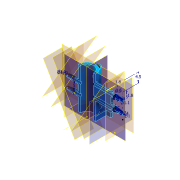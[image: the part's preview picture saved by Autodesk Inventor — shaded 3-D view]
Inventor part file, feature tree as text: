
AUTODESK INVENTOR PART (.ipt)
format: ipt  version: 2021 (Build 250183000, 183)  size: 432,128 bytes
history: native  units: in
note: dims shown in document units (in); Inventor stores cm internally (conversion verified against a paired STEP export)
features: plane x17, sketch x16, extrude x15, projected_geometry x7, mirror x5, revolve x4, split x2, fillet x2, boolean_combine x1
ambient origin geometry x8: Origin, YZ Plane, XZ Plane, XY Plane, X Axis, Y Axis, Z Axis, Center Point
bodies: Solid1 (feature_tree), Solid2 (feature_tree), Solid4 (feature_tree), Solid6 (feature_tree), Solid11 (feature_tree)
feature tree (69):
  extrude  "Extrusion1"  Depth=0.315in
  plane  "Work Plane1"
  sketch  "Sketch2"  dims[d2=0.748in d3=0.0in d4=0.5118in]
  extrude  "Extrusion2"  Depth=0.5118in
  extrude  "Extrusion3"  Depth=0.0709in
  sketch  "Sketch3"  dims[d5=0.0709in d7=0.0709in]
  revolve  "Revolution1"  [1 undecoded]
  revolve  "Revolution3"  [1 undecoded]
  plane  "Work Plane2"
  plane  "Work Plane7"
  extrude  "Extrusion4"  Depth=0.0472in
  extrude  "Extrusion5"  Depth=0.0551in
  sketch  "Sketch6"  dims[d20=0.8268in d21=0.0in d23=0.0472in]
  revolve  "Revolution5"  [1 undecoded]
  plane  "Work Plane8"
  plane  "Work Plane9"
  plane  "Work Plane10"
  plane  "Work Plane14"
  split  "Split7"
  mirror  "Mirror1"
  mirror  "Mirror2"
  revolve  "Revolution9"  Angle=90.0deg
  plane  "Work Plane17"
  extrude  "Extrusion9"  TaperAngle=30.0deg  [1 undecoded]
  plane  "Work Plane18"
  extrude  "Extrusion10"  Depth=0.2756in
  mirror  "Mirror3"
  extrude  "Extrusion16"  Depth=0.0709in
  extrude  "Extrusion17"  Depth=0.0197in
  mirror  "Mirror4"
  mirror  "Mirror5"
  extrude  "Extrusion18"  Depth=0.3937in
  extrude  "Extrusion19"  Depth=0.0551in
  plane  "Work Plane23"
  extrude  "Extrusion20"  Depth=0.0197in
  fillet  "Fillet5"  Radius=0.1969in
  fillet  "Fillet6"  [1 undecoded]
  extrude  "Extrusion21"  Depth=0.3937in
  extrude  "Extrusion22"  TaperAngle=90.0deg  [1 undecoded]
  extrude  "Extrusion23"  [1 undecoded]
  boolean_combine  "Combine1"
  split  "Split10"
  sketch  "Sketch1"  dims[d0=0.2354in d1=0.315in]
  sketch  "Sketch4"  dims[d9=0.1772in d14=0.8268in d15=0.0in]
  sketch  "Sketch5"  dims[d16=0.0197in d18=0.0197in]
  plane  "Work Plane11"
  plane  "Work Plane12"
  plane  "Work Plane13"
  sketch  "Sketch12"  dims[d30=0.0472in d34=0.0551in]
  sketch  "Sketch13"  dims[d35=0.0433in d38=0.0551in]
  plane  "Work Plane19"
  sketch  "Sketch20"  dims[d41=0.0394in d42=90.0deg]
  sketch  "Sketch21"  dims[d44=90.0deg d46=30.0deg]
  plane  "Work Plane20"
  plane  "Work Plane21"
  plane  "Work Plane22"
  sketch  "Sketch22"  dims[d51=-0.2362in d52=0.2756in]
  sketch  "Sketch23"  dims[d53=0.0709in d54=0.0709in]
  sketch  "Sketch24"  dims[d56=0.3937in d57=0.0in d58=0.0197in]
  sketch  "Sketch25"  dims[d60=0.3937in d61=0.0in d62=0.0433in]
  sketch  "Sketch26"  dims[d63=0.0551in d64=0.0472in]
  sketch  "Sketch27"  dims[d71=90.0deg d73=-0.2061in d74=-0.4173in d75=-0.5945in d81=0.1969in d82=0.1969in d103=-0.1969in d106=0.7874in d108=0.1969in d109=0.3937in d111=0.3937in d113=90.0deg d114=-0.1969in d118=0.0197in d119=0.3937in d120=0.0in d121=0.0in d122=0.0in d123=0.0197in d124=-0.1181in d136=0.5118in d137=0.0in d143=0.0197in d144=0.374in d145=0.0in d161=0.315in d162=0.7087in d163=0.0787in d164=0.0in d165=0.0394in d166=0.0787in d167=0.0394in d168=0.0787in d169=0.0in d170=0.0394in d171=0.0in d172=0.0787in d173=0.0in d174=0.4331in d175=0.0512in d176=0.3937in d177=0.0in d178=0.0197in d179=0.0197in d180=0.2953in d181=0.0in d184=0.0984in d185=0.0in d187=0.3937in d188=0.0in d190=0.1772in d191=0.3937in d192=0.1378in d193=0.1378in d194=0.1181in d195=0.0197in d104=0.0344in d105=0.0197in d189=0.0197in]
  projected_geometry  "Project Cut Edges1"
  projected_geometry  "Project Cut Edges6"
  projected_geometry  "Project Cut Edges7"
  projected_geometry  "Project Cut Edges8"
  projected_geometry  "Project Cut Edges9"
  projected_geometry  "Project Cut Edges10"
  projected_geometry  "Project Cut Edges11"
note: 7 required parameter values undecoded (feature->parameter linkage not recoverable at this tier; creation-order binding heuristic only, values carry confidence <= 0.55)